# Revit family: 48087 Контейнерная площадка для ТБО «МАФ - 6» без хозблока Хоббика
name_source: partatom
category: Антураж
revit_build: Autodesk Revit 2018 (Build: 20180423_1000(x64)
units: mm (PartAtom-declared; Revit-internal decimal feet)

## family parameters
Всегда вертикально = Да
Источник визуального образа = Геометрия семейства
На основе рабочей плоскости = Нет
Общий = Нет
При загрузке вырезать с полостями = Нет
Точка расчета площади = Нет

## types (6) — shared parameters
URL = https://hobbyka.ru
Артикул товара = Арт. 48087
Высота = 2200 мм
Группа модели = Контейнерные площадки для ТБО
Изготовитель = ООО «Хоббика»
Материал изделия = Сталь
Цвет каркаса = Сталь
Ширина = 1800 мм

## per-type parameters (varying)
| type | Длина | Изображение типоразмера | На 1 контейнер | На 2 контейнера | На 3 контейнера | На 4 контейнера | На 5 контейнеров | На 6 контейнеров | Описание |
| На 1 контейнер | 2000 мм | Контейнерная площадка для ТБО «МАФ - 6» без хозблока Арт 48087 3 контейнера.jpg | Да | Нет | Нет | Нет | Нет | Нет | Контейнерная площадка для ТБО «МАФ-6» без хозблока. Версия 2,0 м (на 1 контейнер) |
| На 2 контейнера | 3500 мм | Контейнерная площадка для ТБО «МАФ - 6» без хозблока Арт 48087 3 контейнера.jpg | Нет | Да | Нет | Нет | Нет | Нет | Контейнерная площадка для ТБО «МАФ-6» без хозблока. Версия 3,5 м (на 2 контейнера) |
| На 3 контейнера | 5000 мм | Контейнерная площадка для ТБО «МАФ - 6» без хозблока Арт 48087 3 контейнера.jpg | Нет | Нет | Да | Нет | Нет | Нет | Контейнерная площадка для ТБО «МАФ-6» без хозблока. Версия 5,0 м (на 3 контейнера) |
| На 4 контейнера | 6500 мм | Контейнерная площадка для ТБО «МАФ - 6» без хозблока Арт 48087 5 контейнеров.jpg | Нет | Нет | Нет | Да | Нет | Нет | Контейнерная площадка для ТБО «МАФ-6» без хозблока. Версия 6,5 м (на 4 контейнера) |
| На 5 контейнеров | 8000 мм | Контейнерная площадка для ТБО «МАФ - 6» без хозблока Арт 48087 5 контейнеров.jpg | Нет | Нет | Нет | Нет | Да | Нет | Контейнерная площадка для ТБО «МАФ-6» без хозблока. Версия 8,0 м (на 5 контейнеров) |
| На 6 контейнеров | 9500 мм | Контейнерная площадка для ТБО «МАФ - 6» без хозблока Арт 48087 5 контейнеров.jpg | Нет | Нет | Нет | Нет | Нет | Да | Контейнерная площадка для ТБО «МАФ-6» без хозблока. Версия 9,5 м (на 6 контейнеров) |
